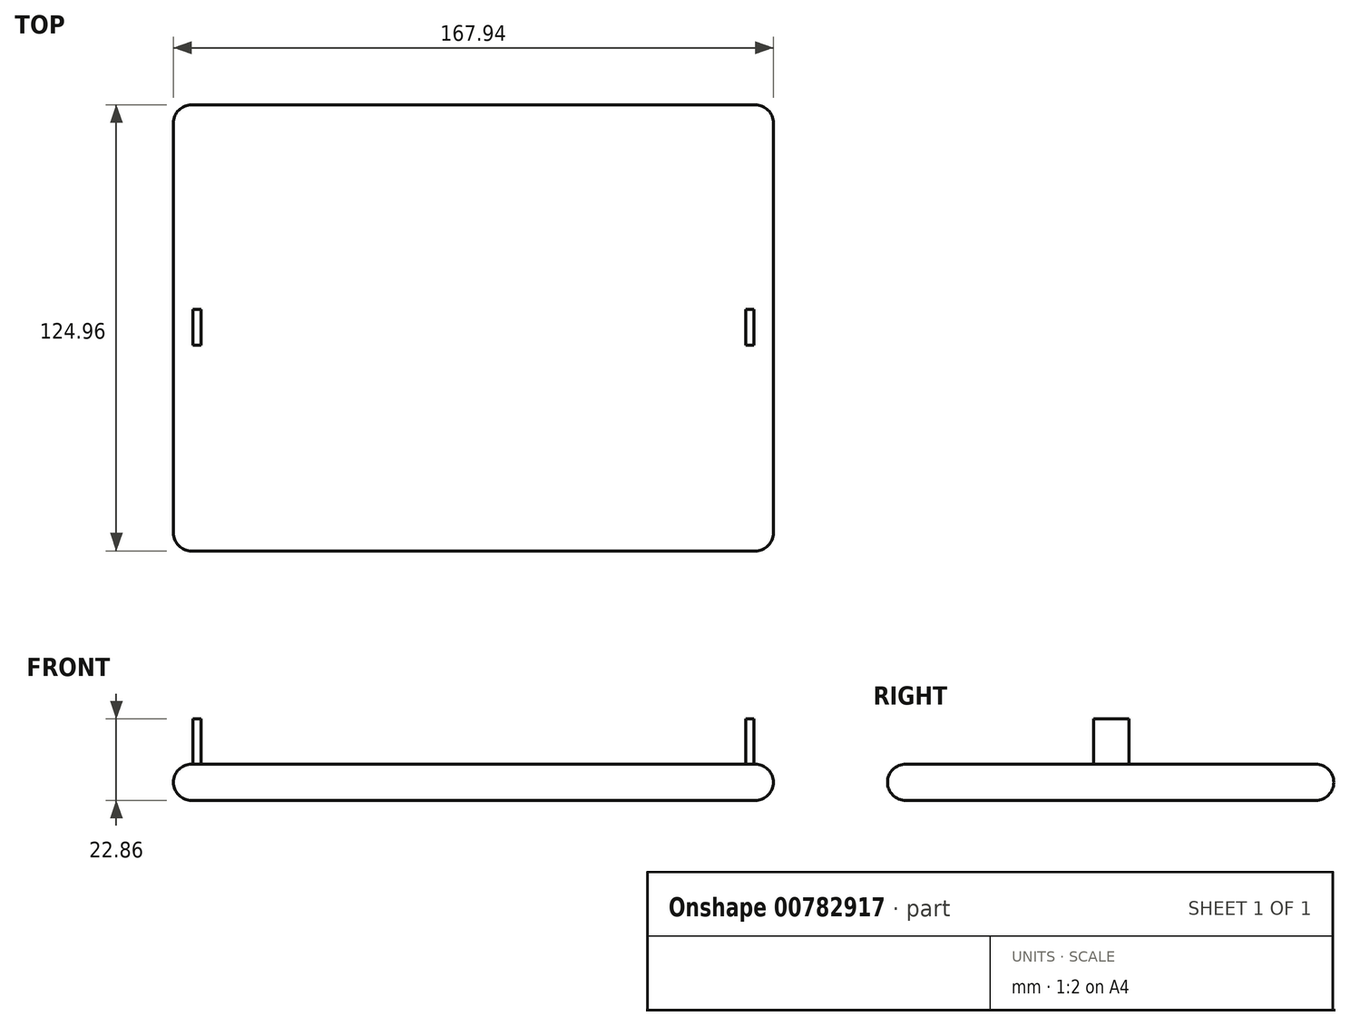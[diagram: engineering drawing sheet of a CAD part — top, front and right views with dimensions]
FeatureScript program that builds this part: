
annotation { "Feature Type Name" : "Feature", "Feature Type Description" : "" }
export const myFeature = defineFeature(function(context is Context, id is Id, definition is map)
    precondition{}
    {
        {
            var Q0;
            Q0=qCreatedBy(makeId("Front.planeOp"),FACE);
            var sketch = newSketch(context, id + "F0", { "sketchPlane" : qUnion([Q0])});
            skLineSegment(sketch, "E0.bottom", {"start": v(-83.97, 5.08) * mm, "end": v(83.97, 5.08) * mm});
            skLineSegment(sketch, "E0.top", {"start": v(-83.97, -5.08) * mm, "end": v(83.97, -5.08) * mm});
            skLineSegment(sketch, "E0.left", {"start": v(-83.97, 5.08) * mm, "end": v(-83.97, -5.08) * mm});
            skLineSegment(sketch, "E0.right", {"start": v(83.97, 5.08) * mm, "end": v(83.97, -5.08) * mm});
            skPoint(sketch, "E0.middle", {"position": v(0, 0) * mm});
            skSolve(sketch);
        }
        {
            var Q0;
            Q0=makeQuery(id+"F0.imprint","IMPRINT",FACE,{"disambiguationData":[TD([[makeQuery(id+"F0.imprint","IMPRINT",EDGE,{"derivedFrom":sQuery(id+"F0.wireOp",EDGE,"E0.bottom")}),-1.0]])]});
            extrude(context, id + "F1", {"entities" : qUnion([Q0]), "endBound" : BoundingType.SYMMETRIC, "depth" : 124.97 * mm, "offsetDistance" : 25.4 * mm});
        }
        {
            var Q0;
            Q0=makeQuery(id+"F1.opExtrude","SWEPT_FACE",FACE,{"disambiguationData":[OSD([sQuery(id+"F0.wireOp",EDGE,"E0.bottom")])]});
            var sketch = newSketch(context, id + "F2", { "sketchPlane" : qUnion([Q0])});
            skLineSegment(sketch, "E1.bottom", {"start": v(-78.54, 5.17) * mm, "end": v(-76.26, 5.17) * mm});
            skLineSegment(sketch, "E1.top", {"start": v(-78.54, -4.8) * mm, "end": v(-76.26, -4.8) * mm});
            skLineSegment(sketch, "E1.left", {"start": v(-78.54, 5.17) * mm, "end": v(-78.54, -4.8) * mm});
            skLineSegment(sketch, "E1.right", {"start": v(-76.26, 5.17) * mm, "end": v(-76.26, -4.8) * mm});
            skLineSegment(sketch, "E2.MirrorCS", {"start": v(76.26, 5.17) * mm, "end": v(76.26, -4.8) * mm});
            skLineSegment(sketch, "E3.MirrorCS", {"start": v(78.54, 5.17) * mm, "end": v(78.54, -4.8) * mm});
            skLineSegment(sketch, "E4.MirrorCS", {"start": v(78.54, 5.17) * mm, "end": v(76.26, 5.17) * mm});
            skLineSegment(sketch, "E5.MirrorCS", {"start": v(78.54, -4.8) * mm, "end": v(76.26, -4.8) * mm});
            skSolve(sketch);
        }
        {
            var Q0;
            Q0 = qSketchRegion(id + "F2", true);
            extrude(context, id + "F3", {"entities" : qUnion([Q0]), "operationType" : NewBodyOperationType.ADD, "depth" : 12.7 * mm, "offsetDistance" : 25.4 * mm});
        }
        {
            var Q0;
            Q0=makeQuery(id+"F1.opExtrude","CAP_FACE",FACE,{"disambiguationData":[OSD([sQuery(id+"F0.wireOp",EDGE,"E0.bottom"),sQuery(id+"F0.wireOp",EDGE,"E0.top"),sQuery(id+"F0.wireOp",EDGE,"E0.left"),sQuery(id+"F0.wireOp",EDGE,"E0.right")])],"isStart":false});
            var Q1;
            Q1=makeQuery(id+"F1.opExtrude","SWEPT_EDGE",EDGE,{"disambiguationData":[OSD([sQuery(id+"F0.wireOp",EDGE,"E0.bottom"),sQuery(id+"F0.wireOp",EDGE,"E0.right")])]});
            var Q2;
            Q2=makeQuery(id+"F1.opExtrude","SWEPT_EDGE",EDGE,{"disambiguationData":[OSD([sQuery(id+"F0.wireOp",EDGE,"E0.bottom"),sQuery(id+"F0.wireOp",EDGE,"E0.left")])]});
            var Q3;
            Q3=makeQuery(id+"F1.opExtrude","CAP_EDGE",EDGE,{"disambiguationData":[OSD([sQuery(id+"F0.wireOp",EDGE,"E0.bottom")])],"isStart":true});
            var Q4;
            Q4=makeQuery(id+"F1.opExtrude","SWEPT_FACE",FACE,{"disambiguationData":[OSD([sQuery(id+"F0.wireOp",EDGE,"E0.top")])]});
            var Q5;
            Q5=makeQuery(id+"F1.opExtrude","CAP_EDGE",EDGE,{"disambiguationData":[OSD([sQuery(id+"F0.wireOp",EDGE,"E0.right")])],"isStart":true});
            var Q6;
            Q6=makeQuery(id+"F1.opExtrude","CAP_EDGE",EDGE,{"disambiguationData":[OSD([sQuery(id+"F0.wireOp",EDGE,"E0.left")])],"isStart":true});
            fillet(context, id + "F4", {"entities" : qUnion([Q0, Q1, Q2, Q3, Q4, Q5, Q6]), "radius" : 5.08 * mm, "tangentPropagation" : true, "allowEdgeOverflow" : false});
        }
    });
